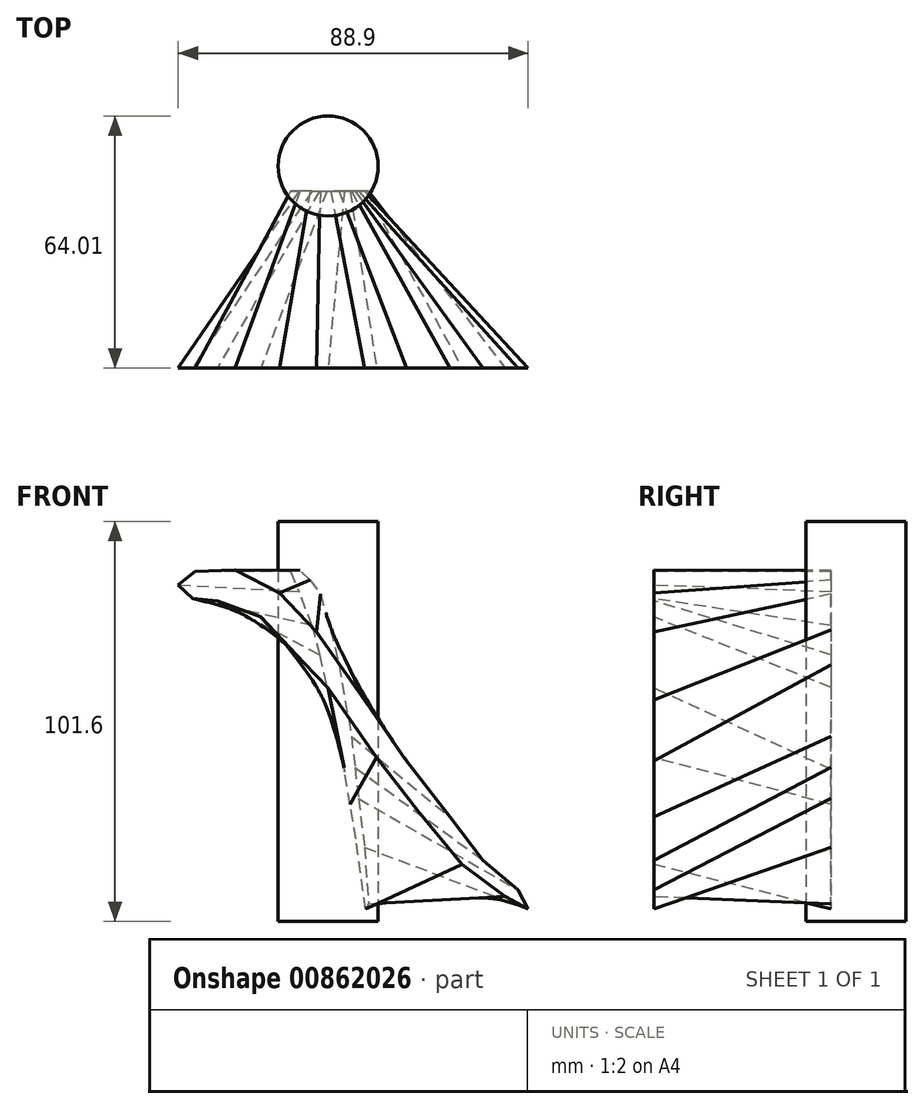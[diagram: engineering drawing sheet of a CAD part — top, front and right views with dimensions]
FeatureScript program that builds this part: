
annotation { "Feature Type Name" : "Feature", "Feature Type Description" : "" }
export const myFeature = defineFeature(function(context is Context, id is Id, definition is map)
    precondition{}
    {
        {
            var Q0;
            Q0=qCreatedBy(makeId("Top.planeOp"),FACE);
            var sketch = newSketch(context, id + "F0", { "sketchPlane" : qUnion([Q0])});
            skCircle(sketch, "E0", {"center": v(0, 0) * mm, "radius": 12.7 * mm});
            skSolve(sketch);
        }
        {
            var Q0;
            Q0=makeQuery(id+"F0.imprint","IMPRINT",FACE,{"disambiguationData":[TD([[makeQuery(id+"F0.imprint","IMPRINT",EDGE,{"derivedFrom":sQuery(id+"F0.wireOp",EDGE,"E0")}),1.0]])]});
            extrude(context, id + "F1", {"entities" : qUnion([Q0]), "depth" : 101.6 * mm, "offsetDistance" : 25.4 * mm});
        }
        {
            var Q0;
            Q0=qCreatedBy(makeId("Front.planeOp"),FACE);
            cPlane(context, id + "F2", {"entities" : qUnion([Q0]), "cplaneType" : CPlaneType.OFFSET, "offset" : 6.35 * mm, "width" : 152.4 * mm, "height" : 152.4 * mm});
        }
        {
            var Q0;
            Q0=qCreatedBy(id+"F2.planeOp",FACE);
            var sketch = newSketch(context, id + "F3", { "sketchPlane" : qUnion([Q0])});
            skLineSegment(sketch, "E1", {"start": v(-4.61, 86.77) * mm, "end": v(-7.17, 89.21) * mm});
            skLineSegment(sketch, "E2", {"start": v(-7.17, 89.21) * mm, "end": v(-9.52, 88.9) * mm});
            skLineSegment(sketch, "E3", {"start": v(10.25, 4.5) * mm, "end": v(9.53, 3.18) * mm});
            skLineSegment(sketch, "E4", {"start": v(9.53, 3.18) * mm, "end": v(7.05, 20.93) * mm});
            skLineSegment(sketch, "E5", {"start": v(-9.52, 88.9) * mm, "end": v(-7.39, 83.71) * mm});
            skLineSegment(sketch, "E6", {"start": v(-4.61, 86.77) * mm, "end": v(-2, 83.15) * mm});
            skLineSegment(sketch, "E7", {"start": v(-2, 83.15) * mm, "end": v(0.65, 74.12) * mm});
            skLineSegment(sketch, "E8", {"start": v(0.65, 74.12) * mm, "end": v(2.76, 65.1) * mm});
            skLineSegment(sketch, "E9", {"start": v(2.76, 65.1) * mm, "end": v(5.91, 47.04) * mm});
            skLineSegment(sketch, "E10", {"start": v(5.91, 47.04) * mm, "end": v(7.7, 31.25) * mm});
            skLineSegment(sketch, "E11", {"start": v(7.7, 31.25) * mm, "end": v(9.23, 18.82) * mm});
            skLineSegment(sketch, "E12", {"start": v(9.23, 18.82) * mm, "end": v(10.25, 4.5) * mm});
            skLineSegment(sketch, "E13", {"start": v(-4.1, 75.15) * mm, "end": v(-7.39, 83.71) * mm});
            skLineSegment(sketch, "E14", {"start": v(7.05, 20.93) * mm, "end": v(4.1, 38.57) * mm});
            skLineSegment(sketch, "E15", {"start": v(4.1, 38.57) * mm, "end": v(1.5, 51.2) * mm});
            skLineSegment(sketch, "E16", {"start": v(-4.1, 75.15) * mm, "end": v(-2.16, 67.7) * mm});
            skLineSegment(sketch, "E17", {"start": v(-2.16, 67.7) * mm, "end": v(1.5, 51.2) * mm});
            skSolve(sketch);
        }
        {
            var Q0;
            Q0=qCreatedBy(makeId("Front.planeOp"),FACE);
            cPlane(context, id + "F4", {"entities" : qUnion([Q0]), "cplaneType" : CPlaneType.OFFSET, "offset" : 51.3 * mm, "width" : 152.4 * mm, "height" : 152.4 * mm});
        }
        {
            var Q0;
            Q0=qCreatedBy(id+"F4.planeOp",FACE);
            var sketch = newSketch(context, id + "F5", { "sketchPlane" : qUnion([Q0])});
            skLineSegment(sketch, "E18", {"start": v(-38.1, 85.43) * mm, "end": v(-34.5, 82) * mm});
            skLineSegment(sketch, "E19", {"start": v(-34.5, 82) * mm, "end": v(-28.13, 81.47) * mm});
            skLineSegment(sketch, "E20", {"start": v(50.8, 3.17) * mm, "end": v(48.22, 8.03) * mm});
            skLineSegment(sketch, "E21", {"start": v(50.8, 3.17) * mm, "end": v(44.98, 6.3) * mm});
            skLineSegment(sketch, "E22", {"start": v(44.98, 6.3) * mm, "end": v(34.04, 14.45) * mm});
            skLineSegment(sketch, "E23", {"start": v(12.25, 41.6) * mm, "end": v(0, 59.27) * mm});
            skLineSegment(sketch, "E24", {"start": v(-38.1, 85.43) * mm, "end": v(-33.8, 88.9) * mm});
            skLineSegment(sketch, "E25", {"start": v(-33.8, 88.9) * mm, "end": v(-23.64, 89.24) * mm});
            skLineSegment(sketch, "E26", {"start": v(30.93, 26.51) * mm, "end": v(39.4, 15.55) * mm});
            skLineSegment(sketch, "E27", {"start": v(39.4, 15.55) * mm, "end": v(48.22, 8.03) * mm});
            skLineSegment(sketch, "E28", {"start": v(-6.1, 65.66) * mm, "end": v(0, 59.27) * mm});
            skLineSegment(sketch, "E29", {"start": v(12.25, 41.6) * mm, "end": v(22.73, 28.18) * mm});
            skLineSegment(sketch, "E30", {"start": v(22.73, 28.18) * mm, "end": v(34.04, 14.45) * mm});
            skLineSegment(sketch, "E31", {"start": v(30.93, 26.51) * mm, "end": v(19.91, 40.76) * mm});
            skLineSegment(sketch, "E32", {"start": v(19.91, 40.76) * mm, "end": v(9.2, 56.32) * mm});
            skLineSegment(sketch, "E33", {"start": v(-23.64, 89.24) * mm, "end": v(-12.36, 83.47) * mm});
            skLineSegment(sketch, "E34", {"start": v(-12.36, 83.47) * mm, "end": v(-2.93, 73.52) * mm});
            skLineSegment(sketch, "E35", {"start": v(-2.93, 73.52) * mm, "end": v(9.2, 56.32) * mm});
            skLineSegment(sketch, "E36", {"start": v(-6.1, 65.66) * mm, "end": v(-17.07, 77.3) * mm});
            skLineSegment(sketch, "E37", {"start": v(-17.07, 77.3) * mm, "end": v(-28.13, 81.47) * mm});
            skSolve(sketch);
        }
        {
            var Q0;
            Q0 = qSketchRegion(id + "F3", true);
            var Q1;
            Q1 = qSketchRegion(id + "F5", true);
            loft(context, id + "F6", {"sheetProfilesArray" : [{ "sheetProfileEntities" : qUnion([Q0]) }, { "sheetProfileEntities" : qUnion([Q1]) }]});
        }
    });
